# Revit family: IS_Melange_A4264_BIM_DE
name_source: partatom
category: Plumbing Fixtures
revit_build: Autodesk Revit MEP 2016 (Build: 20161004_0715(x64)
units: mm (PartAtom-declared; Revit-internal decimal feet)

## family parameters
Cut with Voids When Loaded = No
Host = Face
OmniClass Number = 23.45.55.17
OmniClass Title = Mixing Faucets
Part Type = Normal
Room Calculation Point = No
Round Connector Dimension = Use Diameter
Shared = Yes

## types (1)
- A4264AA - MELANGE BSN MXR B-IN CHROME KIT2 HORIZ.
    Accessories = www.idealstandard.de\ersatzteile
    AreaUnits = millimeters
    Assembly Code = C1030200
    AssetType = Fixed
    BIMObjectName = ISI_IdealStandard_MixerTaps_MELANGE_A4264AA
    BarCode = 4015413316576
    Brand = Ideal Standard
    CWFU = 0
    CodePerformance = 0
    Color = Chrome
    ConnectionType = Plumbing
    Cost = 0 $
    CurrencyUnit = €
    Default Elevation = 800 mm  [stored 2.62467 ft]
    Description = Melange Basin Mixer Built-In  Kit2
    DurationUnit = year
    ExpectedLife = 25
    FaucetFunction = MIXED
    FaucetOperation = LEVERHANDLE
    FaucetType = PILLAR
    Features = MELANGE wall mounted basin mixer
    Finish = Chrome
    GrossWeight = 2,052 kg
    HWFU = 0
    IfcExportAs = IfcValveType
    IfcExportType = FAUCET
    InstallationDate = 1900-12-31T23:59:59
    InstallationInstructions = www.idealstandard.de\produkte
    LinearUnits = millimeters
    ManufacturerURL = www.idealstandard.de
    Material = Brass
    Model = A4264AA
    ModelNumber = A4264AA
    ModelReference = IS Wand-WT-Armatur Bausatz 2 MELANGE Chrom
    NBSDescription = Water supply fittings for wash basins and troughs
    NBSReference = 45-35-70/371
    Name = ISI_IdealStandard_MixerTaps_MELANGE_A4264AA
    NettWeight = 2,052 kg
    NominalDepth = 0 mm  [stored 0 ft]
    NominalHeight = 128 mm
    NominalLength = 231 mm
    NominalWidth = 225 mm
    ProductInformation = www.idealstandard.de
    Shape = Sculptured
    Size = 231 x 225 x 128 mm
    Space = Internal
    SpareParts = www.idealstandard.de/ersatzteile
    TestPressure = 10 Bar
    URL = www.idealstandard.de
    Uniclass2015Code = Pr_40_20_87_98
    Uniclass2015Title = Washbasin taps
    Uniclass2015Version = Products v1.1
    ValveOperation = lever
    Version = 1
    VolumeUnits = Litres
    WFU = 0
    WorkingPressure = 1-5 Bar

note: [stored X ft] marks values corroborated as IEEE doubles in the binary element streams (Revit-internal decimal feet)

## geometry (parser evidence)
native form markers: Blend x4, Sweep x1
no freeform markers — native parametric forms only
